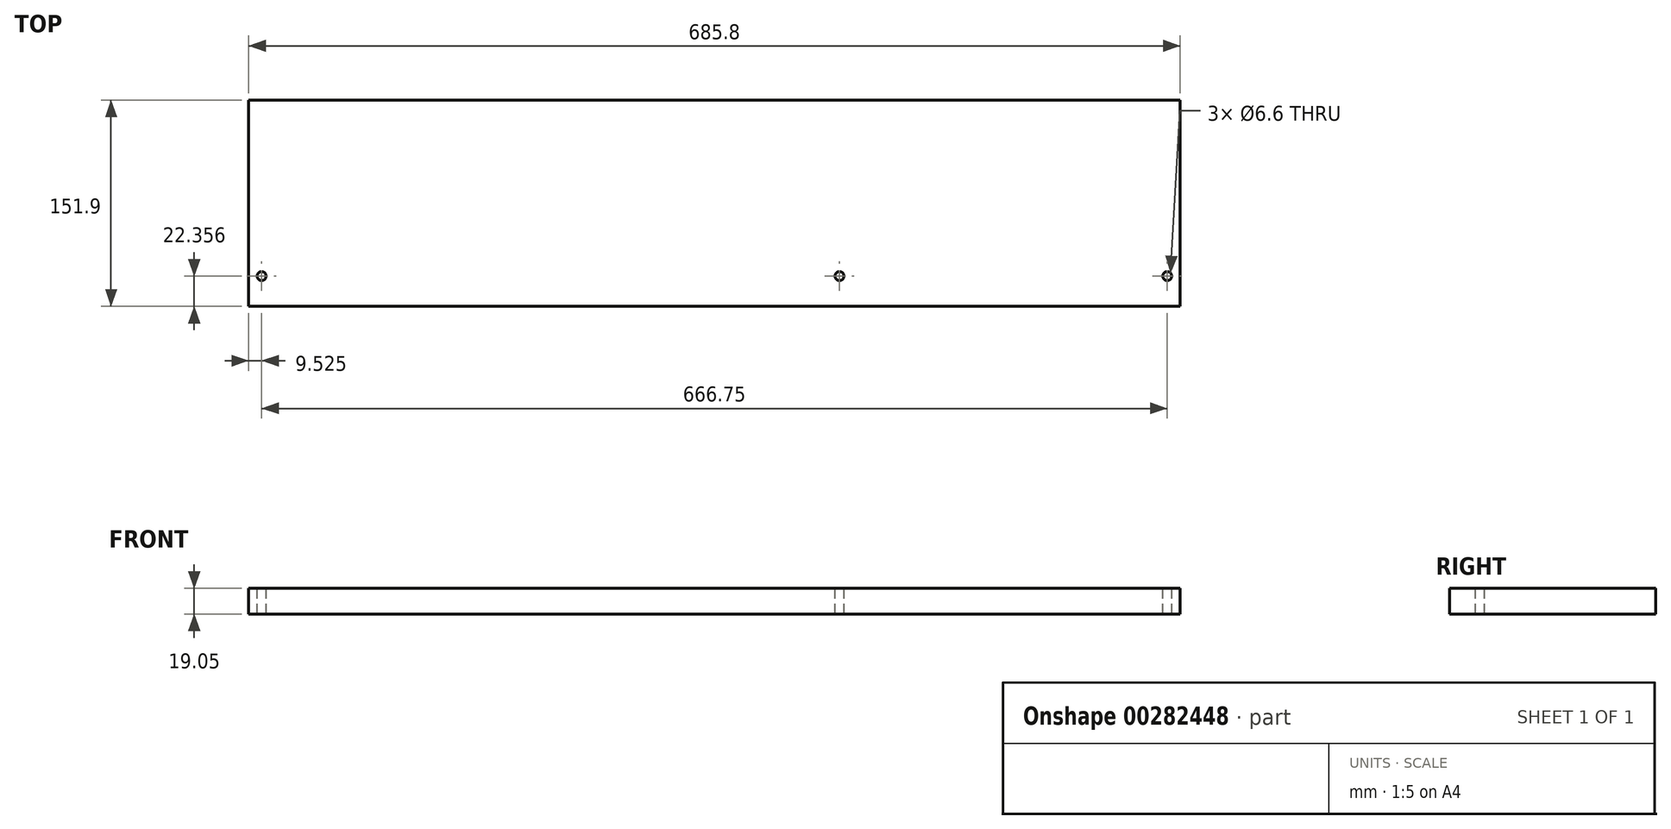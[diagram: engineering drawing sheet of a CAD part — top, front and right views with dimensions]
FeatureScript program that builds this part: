
annotation { "Feature Type Name" : "Feature", "Feature Type Description" : "" }
export const myFeature = defineFeature(function(context is Context, id is Id, definition is map)
    precondition{}
    {
        {
            var Q0;
            Q0=qCreatedBy(makeId("Top.planeOp"),FACE);
            var sketch = newSketch(context, id + "F0", { "sketchPlane" : qUnion([Q0])});
            skLineSegment(sketch, "E0.bottom", {"start": v(-342.9, -75.95) * mm, "end": v(342.9, -75.95) * mm});
            skLineSegment(sketch, "E0.top", {"start": v(-342.9, 75.95) * mm, "end": v(342.9, 75.95) * mm});
            skLineSegment(sketch, "E0.left", {"start": v(-342.9, -75.95) * mm, "end": v(-342.9, 75.95) * mm});
            skLineSegment(sketch, "E0.right", {"start": v(342.9, -75.95) * mm, "end": v(342.9, 75.95) * mm});
            skPoint(sketch, "E0.middle", {"position": v(0, 0) * mm});
            skLineSegment(sketch, "E1", {"start": v(-342.9, 0) * mm, "end": v(-323.85, 0) * mm, "construction": true});
            skPoint(sketch, "E1.endSnap0", {"position": v(-342.9, 0) * mm});
            skLineSegment(sketch, "E2", {"start": v(-323.85, 0) * mm, "end": v(82.55, 0) * mm, "construction": true});
            skLineSegment(sketch, "E3", {"start": v(82.55, 0) * mm, "end": v(101.6, 0) * mm, "construction": true});
            skLineSegment(sketch, "E4", {"start": v(101.6, 0) * mm, "end": v(323.85, 0) * mm, "construction": true});
            skLineSegment(sketch, "E5", {"start": v(323.85, 0) * mm, "end": v(342.9, 0) * mm, "construction": true});
            skLineSegment(sketch, "E6", {"start": v(-323.85, 75.95) * mm, "end": v(-323.85, -75.95) * mm, "construction": true});
            skLineSegment(sketch, "E7", {"start": v(-333.38, 75.95) * mm, "end": v(-333.38, -75.95) * mm, "construction": true});
            skPoint(sketch, "E7.startSnap0", {"position": v(-333.38, 0) * mm});
            skLineSegment(sketch, "E8", {"start": v(101.6, 75.95) * mm, "end": v(101.6, -75.95) * mm, "construction": true});
            skLineSegment(sketch, "E9", {"start": v(82.55, 75.95) * mm, "end": v(82.55, -75.95) * mm, "construction": true});
            skLineSegment(sketch, "E10", {"start": v(92.08, 75.95) * mm, "end": v(92.08, -75.95) * mm, "construction": true});
            skPoint(sketch, "E10.startSnap0", {"position": v(92.08, 0) * mm});
            skLineSegment(sketch, "E11", {"start": v(323.85, 75.95) * mm, "end": v(323.85, -75.95) * mm, "construction": true});
            skLineSegment(sketch, "E12", {"start": v(333.38, 75.95) * mm, "end": v(333.38, -75.95) * mm, "construction": true});
            skPoint(sketch, "E12.startSnap0", {"position": v(333.38, 0) * mm});
            skSolve(sketch);
        }
        {
            var Q0;
            Q0 = qSketchRegion(id + "F0", true);
            extrude(context, id + "F1", {"entities" : qUnion([Q0]), "depth" : 19.05 * mm});
        }
        {
            var Q0;
            Q0=makeQuery(id+"F1.opExtrude","CAP_FACE",FACE,{"disambiguationData":[OSD([sQuery(id+"F0.wireOp",EDGE,"E0.bottom"),sQuery(id+"F0.wireOp",EDGE,"E0.top"),sQuery(id+"F0.wireOp",EDGE,"E0.left"),sQuery(id+"F0.wireOp",EDGE,"E0.right")])],"isStart":false});
            var sketch = newSketch(context, id + "F2", { "sketchPlane" : qUnion([Q0])});
            skLineSegment(sketch, "E13.0", {"start": v(-333.38, 75.95) * mm, "end": v(-333.38, -75.95) * mm, "construction": true});
            skLineSegment(sketch, "E14.0", {"start": v(92.08, 75.95) * mm, "end": v(92.08, -75.95) * mm, "construction": true});
            skLineSegment(sketch, "E15.0", {"start": v(333.38, 75.95) * mm, "end": v(333.38, -75.95) * mm, "construction": true});
            skLineSegment(sketch, "E16.0", {"start": v(-323.85, 0) * mm, "end": v(82.55, 0) * mm, "construction": true});
            skLineSegment(sketch, "E17.0", {"start": v(101.6, 0) * mm, "end": v(323.85, 0) * mm, "construction": true});
            skLineSegment(sketch, "E18.0", {"start": v(82.55, 0) * mm, "end": v(101.6, 0) * mm, "construction": true});
            skLineSegment(sketch, "E19.0", {"start": v(323.85, 0) * mm, "end": v(342.9, 0) * mm, "construction": true});
            skLineSegment(sketch, "E20.0", {"start": v(-342.9, 0) * mm, "end": v(-323.85, 0) * mm, "construction": true});
            skCircle(sketch, "E21", {"center": v(-333.38, -53.6) * mm, "radius": 3.3 * mm});
            skCircle(sketch, "E22", {"center": v(92.08, -53.6) * mm, "radius": 3.3 * mm});
            skCircle(sketch, "E23", {"center": v(333.38, -53.6) * mm, "radius": 3.3 * mm});
            skLineSegment(sketch, "E24", {"start": v(-333.38, -75.95) * mm, "end": v(-333.38, -56.9) * mm, "construction": true});
            skLineSegment(sketch, "E25", {"start": v(92.08, -75.95) * mm, "end": v(92.08, -56.9) * mm, "construction": true});
            skLineSegment(sketch, "E26", {"start": v(333.38, -75.95) * mm, "end": v(333.38, -56.9) * mm, "construction": true});
            skSolve(sketch);
        }
        {
            var Q0;
            Q0 = qSketchRegion(id + "F2", true);
            extrude(context, id + "F3", {"entities" : qUnion([Q0]), "operationType" : NewBodyOperationType.REMOVE, "oppositeDirection" : true, "depth" : 19.05 * mm});
        }
    });
